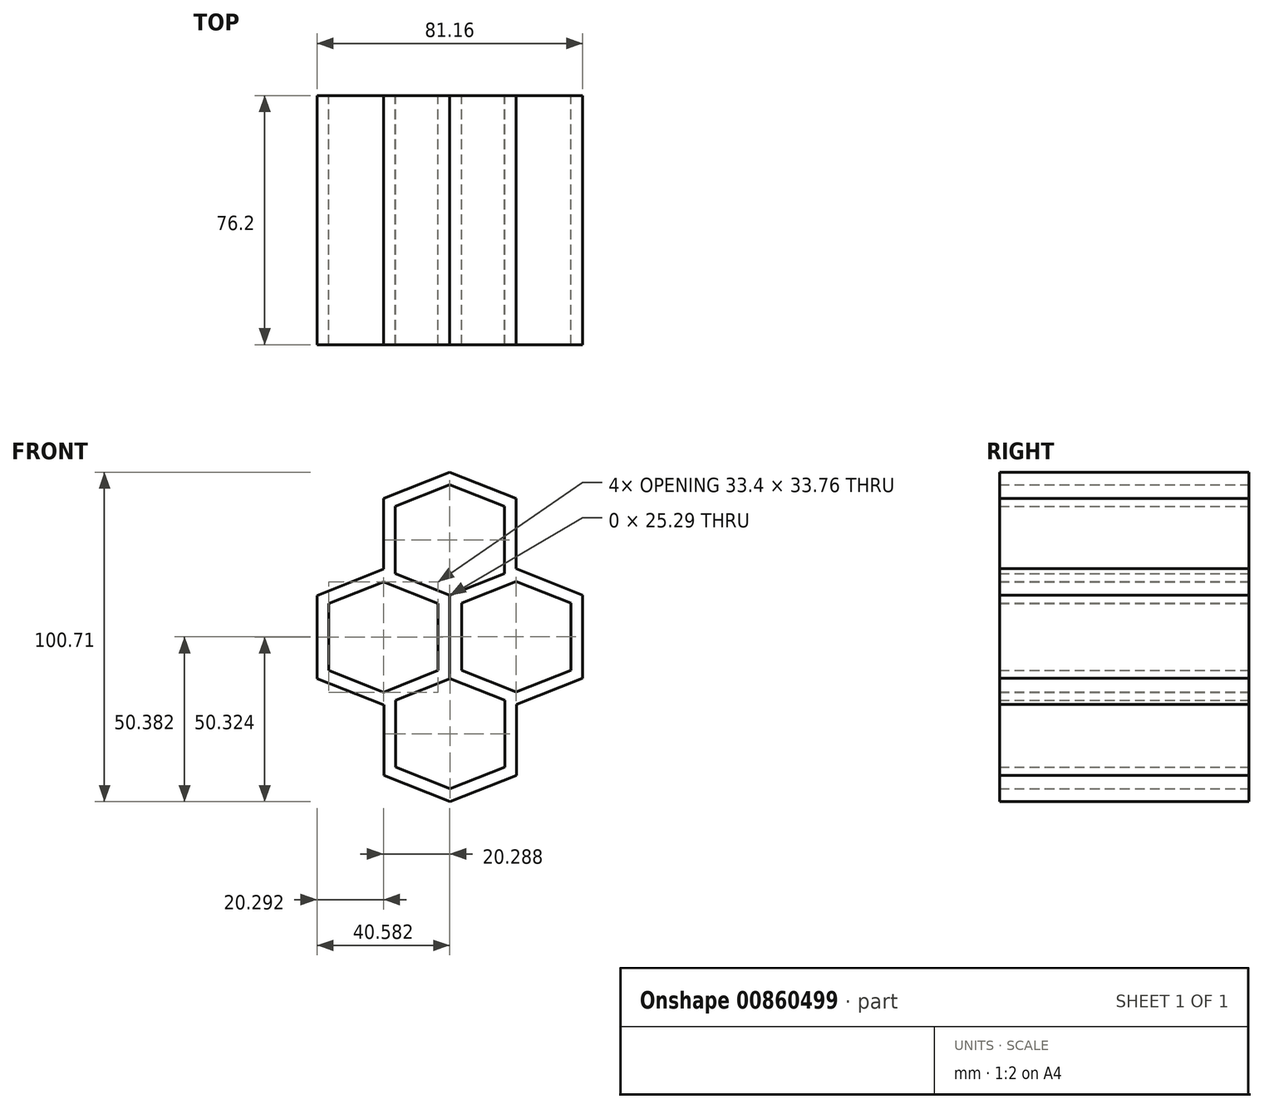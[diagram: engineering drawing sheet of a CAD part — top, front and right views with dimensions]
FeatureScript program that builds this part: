
annotation { "Feature Type Name" : "Feature", "Feature Type Description" : "" }
export const myFeature = defineFeature(function(context is Context, id is Id, definition is map)
    precondition{}
    {
        {
            var Q0;
            Q0=qCreatedBy(makeId("Front.planeOp"),FACE);
            var sketch = newSketch(context, id + "F0", { "sketchPlane" : qUnion([Q0])});
            skLineSegment(sketch, "E0.MirrorCS", {"start": v(-4.08, 37.56) * mm, "end": v(12.62, 30.94) * mm});
            skLineSegment(sketch, "E1.0", {"start": v(-4.08, 41.43) * mm, "end": v(16.21, 33.39) * mm});
            skLineSegment(sketch, "E2", {"start": v(32.68, -0.09) * mm, "end": v(-51.47, -0.09) * mm, "construction": true});
            skPoint(sketch, "E2.endSnap0", {"position": v(-44.43, -0.09) * mm});
            skLineSegment(sketch, "E3", {"start": v(-4.08, 48.57) * mm, "end": v(-4.08, -7.94) * mm, "construction": true});
            skLineSegment(sketch, "E4", {"start": v(-24.46, 20.69) * mm, "end": v(25.85, 20.69) * mm, "construction": true});
            skLineSegment(sketch, "E5", {"start": v(12.62, 30.94) * mm, "end": v(12.62, 20.69) * mm});
            skLineSegment(sketch, "E6", {"start": v(16.21, 33.39) * mm, "end": v(16.21, 20.69) * mm});
            skLineSegment(sketch, "E7.MirrorCS", {"start": v(-4.08, 41.43) * mm, "end": v(-24.37, 33.39) * mm});
            skLineSegment(sketch, "E8.MirrorCS", {"start": v(-4.08, 37.56) * mm, "end": v(-20.78, 30.94) * mm});
            skLineSegment(sketch, "E9.MirrorCS", {"start": v(-20.78, 30.94) * mm, "end": v(-20.78, 20.69) * mm});
            skLineSegment(sketch, "E10.MirrorCS", {"start": v(-24.37, 33.39) * mm, "end": v(-24.37, 20.69) * mm});
            skLineSegment(sketch, "E11.MirrorCS", {"start": v(-20.78, 10.43) * mm, "end": v(-20.78, 20.69) * mm});
            skLineSegment(sketch, "E12.MirrorCS", {"start": v(-24.37, 7.99) * mm, "end": v(-24.37, 20.69) * mm});
            skLineSegment(sketch, "E13.MirrorCS", {"start": v(-4.08, -0.06) * mm, "end": v(-24.37, 7.99) * mm});
            skLineSegment(sketch, "E14.MirrorCS", {"start": v(-4.08, 3.8) * mm, "end": v(-20.78, 10.43) * mm});
            skLineSegment(sketch, "E15.MirrorCS", {"start": v(-4.08, 3.8) * mm, "end": v(12.62, 10.43) * mm});
            skLineSegment(sketch, "E16.MirrorCS", {"start": v(12.62, 10.43) * mm, "end": v(12.62, 20.69) * mm});
            skLineSegment(sketch, "E17.MirrorCS", {"start": v(16.21, 7.99) * mm, "end": v(16.21, 20.69) * mm});
            skLineSegment(sketch, "E18.MirrorCS", {"start": v(-4.08, -0.06) * mm, "end": v(16.21, 7.99) * mm});
            skLineSegment(sketch, "E19.MirrorCS", {"start": v(16.21, 8.04) * mm, "end": v(32.91, 1.42) * mm});
            skLineSegment(sketch, "E20.0", {"start": v(16.21, 11.9) * mm, "end": v(36.5, 3.86) * mm});
            skLineSegment(sketch, "E21", {"start": v(-4.17, -8.84) * mm, "end": v(46.14, -8.84) * mm, "construction": true});
            skLineSegment(sketch, "E22", {"start": v(32.91, 1.42) * mm, "end": v(32.91, -8.84) * mm});
            skLineSegment(sketch, "E23", {"start": v(36.5, 3.86) * mm, "end": v(36.5, -8.84) * mm});
            skLineSegment(sketch, "E24.MirrorCS", {"start": v(16.21, 11.9) * mm, "end": v(-4.08, 3.86) * mm});
            skLineSegment(sketch, "E25.MirrorCS", {"start": v(16.21, 8.04) * mm, "end": v(-0.49, 1.42) * mm});
            skLineSegment(sketch, "E26.MirrorCS", {"start": v(-0.49, 1.42) * mm, "end": v(-0.49, -8.84) * mm});
            skLineSegment(sketch, "E27.MirrorCS", {"start": v(-4.08, 3.86) * mm, "end": v(-4.08, -8.84) * mm});
            skLineSegment(sketch, "E28.MirrorCS", {"start": v(-0.49, -19.1) * mm, "end": v(-0.49, -8.84) * mm});
            skLineSegment(sketch, "E29.MirrorCS", {"start": v(-4.08, -21.54) * mm, "end": v(-4.08, -8.84) * mm});
            skLineSegment(sketch, "E30.MirrorCS", {"start": v(16.21, -29.58) * mm, "end": v(-4.08, -21.54) * mm});
            skLineSegment(sketch, "E31.MirrorCS", {"start": v(16.21, -25.72) * mm, "end": v(-0.49, -19.1) * mm});
            skLineSegment(sketch, "E32.MirrorCS", {"start": v(16.21, -25.72) * mm, "end": v(32.91, -19.1) * mm});
            skLineSegment(sketch, "E33.MirrorCS", {"start": v(32.91, -19.1) * mm, "end": v(32.91, -8.84) * mm});
            skLineSegment(sketch, "E34.MirrorCS", {"start": v(36.5, -21.54) * mm, "end": v(36.5, -8.84) * mm});
            skLineSegment(sketch, "E35.MirrorCS", {"start": v(16.21, -29.58) * mm, "end": v(36.5, -21.54) * mm});
            skLineSegment(sketch, "E36.MirrorCS", {"start": v(-24.37, 7.92) * mm, "end": v(-7.67, 1.3) * mm});
            skLineSegment(sketch, "E37.0", {"start": v(-24.37, 11.79) * mm, "end": v(-4.08, 3.74) * mm});
            skLineSegment(sketch, "E38", {"start": v(-44.75, -8.96) * mm, "end": v(5.56, -8.96) * mm, "construction": true});
            skLineSegment(sketch, "E39", {"start": v(-7.67, 1.3) * mm, "end": v(-7.67, -8.96) * mm});
            skLineSegment(sketch, "E40", {"start": v(-4.08, 3.74) * mm, "end": v(-4.08, -8.96) * mm});
            skLineSegment(sketch, "E41.MirrorCS", {"start": v(-24.37, 11.79) * mm, "end": v(-44.66, 3.74) * mm});
            skLineSegment(sketch, "E42.MirrorCS", {"start": v(-24.37, 7.92) * mm, "end": v(-41.07, 1.3) * mm});
            skLineSegment(sketch, "E43.MirrorCS", {"start": v(-41.07, 1.3) * mm, "end": v(-41.07, -8.96) * mm});
            skLineSegment(sketch, "E44.MirrorCS", {"start": v(-44.66, 3.74) * mm, "end": v(-44.66, -8.96) * mm});
            skLineSegment(sketch, "E45.MirrorCS", {"start": v(-41.07, -19.22) * mm, "end": v(-41.07, -8.96) * mm});
            skLineSegment(sketch, "E46.MirrorCS", {"start": v(-44.66, -21.66) * mm, "end": v(-44.66, -8.96) * mm});
            skLineSegment(sketch, "E47.MirrorCS", {"start": v(-24.37, -29.7) * mm, "end": v(-44.66, -21.66) * mm});
            skLineSegment(sketch, "E48.MirrorCS", {"start": v(-24.37, -25.83) * mm, "end": v(-41.07, -19.22) * mm});
            skLineSegment(sketch, "E49.MirrorCS", {"start": v(-24.37, -25.83) * mm, "end": v(-7.67, -19.22) * mm});
            skLineSegment(sketch, "E50.MirrorCS", {"start": v(-7.67, -19.22) * mm, "end": v(-7.67, -8.96) * mm});
            skLineSegment(sketch, "E51.MirrorCS", {"start": v(-4.08, -21.66) * mm, "end": v(-4.08, -8.96) * mm});
            skLineSegment(sketch, "E52.MirrorCS", {"start": v(-24.37, -29.7) * mm, "end": v(-4.08, -21.66) * mm});
            skLineSegment(sketch, "E53.MirrorCS", {"start": v(-3.93, -21.66) * mm, "end": v(12.77, -28.28) * mm});
            skLineSegment(sketch, "E54.0", {"start": v(-3.93, -17.8) * mm, "end": v(16.36, -25.84) * mm});
            skLineSegment(sketch, "E55", {"start": v(-24.31, -38.54) * mm, "end": v(26, -38.54) * mm, "construction": true});
            skLineSegment(sketch, "E56", {"start": v(12.77, -28.28) * mm, "end": v(12.77, -38.54) * mm});
            skLineSegment(sketch, "E57", {"start": v(16.36, -25.84) * mm, "end": v(16.36, -38.54) * mm});
            skLineSegment(sketch, "E58.MirrorCS", {"start": v(-3.93, -17.8) * mm, "end": v(-24.22, -25.84) * mm});
            skLineSegment(sketch, "E59.MirrorCS", {"start": v(-3.93, -21.66) * mm, "end": v(-20.63, -28.28) * mm});
            skLineSegment(sketch, "E60.MirrorCS", {"start": v(-20.63, -28.28) * mm, "end": v(-20.63, -38.54) * mm});
            skLineSegment(sketch, "E61.MirrorCS", {"start": v(-24.22, -25.84) * mm, "end": v(-24.22, -38.54) * mm});
            skLineSegment(sketch, "E62.MirrorCS", {"start": v(-20.63, -48.8) * mm, "end": v(-20.63, -38.54) * mm});
            skLineSegment(sketch, "E63.MirrorCS", {"start": v(-24.22, -51.24) * mm, "end": v(-24.22, -38.54) * mm});
            skLineSegment(sketch, "E64.MirrorCS", {"start": v(-3.93, -59.28) * mm, "end": v(-24.22, -51.24) * mm});
            skLineSegment(sketch, "E65.MirrorCS", {"start": v(-3.93, -55.42) * mm, "end": v(-20.63, -48.8) * mm});
            skLineSegment(sketch, "E66.MirrorCS", {"start": v(-3.93, -55.42) * mm, "end": v(12.77, -48.8) * mm});
            skLineSegment(sketch, "E67.MirrorCS", {"start": v(12.77, -48.8) * mm, "end": v(12.77, -38.54) * mm});
            skLineSegment(sketch, "E68.MirrorCS", {"start": v(16.36, -51.24) * mm, "end": v(16.36, -38.54) * mm});
            skLineSegment(sketch, "E69.MirrorCS", {"start": v(-3.93, -59.28) * mm, "end": v(16.36, -51.24) * mm});
            skSolve(sketch);
        }
        {
            var Q0;
            Q0 = qSketchRegion(id + "F0", true);
            extrude(context, id + "F1", {"entities" : qUnion([Q0]), "depth" : 76.2 * mm, "offsetDistance" : 25.4 * mm});
        }
    });
